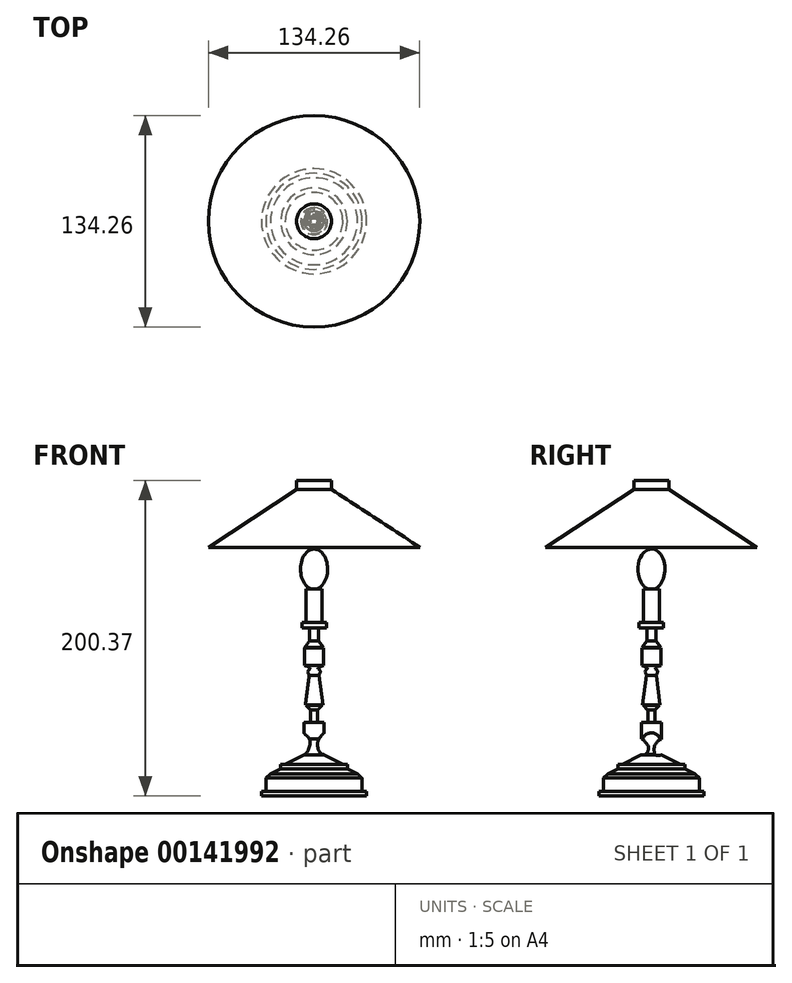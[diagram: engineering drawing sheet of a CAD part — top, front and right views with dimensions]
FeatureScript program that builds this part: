
annotation { "Feature Type Name" : "Feature", "Feature Type Description" : "" }
export const myFeature = defineFeature(function(context is Context, id is Id, definition is map)
    precondition{}
    {
        {
            var Q0;
            Q0=qCreatedBy(makeId("Right.planeOp"),FACE);
            var sketch = newSketch(context, id + "F0", { "sketchPlane" : qUnion([Q0])});
            skLineSegment(sketch, "E0", {"start": v(0, 0) * mm, "end": v(-33.4, 0) * mm});
            skLineSegment(sketch, "E1", {"start": v(-33.4, 0) * mm, "end": v(-33.4, 2.94) * mm});
            skLineSegment(sketch, "E2", {"start": v(-33.4, 2.94) * mm, "end": v(0, 2.94) * mm});
            skLineSegment(sketch, "E3", {"start": v(-30.54, 2.94) * mm, "end": v(-30.54, 11.3) * mm});
            skLineSegment(sketch, "E4", {"start": v(-30.54, 11.3) * mm, "end": v(-27.63, 14.04) * mm});
            skLineSegment(sketch, "E5", {"start": v(-27.63, 14.04) * mm, "end": v(-21.15, 17.21) * mm});
            skLineSegment(sketch, "E6", {"start": v(-21.15, 17.21) * mm, "end": v(-21.15, 20.02) * mm});
            skLineSegment(sketch, "E7", {"start": v(-21.15, 20.02) * mm, "end": v(-18.3, 20.02) * mm});
            skLineSegment(sketch, "E8", {"start": v(-18.3, 20.02) * mm, "end": v(0, 29.2) * mm});
            skLineSegment(sketch, "E9", {"start": v(0, 29.2) * mm, "end": v(0, 0) * mm, "construction": true});
            skLineSegment(sketch, "E10", {"start": v(0, 29.2) * mm, "end": v(0, 0) * mm});
            skSolve(sketch);
        }
        {
            var Q0;
            Q0 = qSketchRegion(id + "F0", true);
            var Q1;
            Q1=sQuery(id+"F0.wireOp",EDGE,"E9");
            revolve(context, id + "F1", {"entities" : qUnion([Q0]), "axis" : qUnion([Q1]), "revolveType" : RevolveType.FULL});
        }
        {
            var Q0;
            Q0=qCreatedBy(makeId("Top.planeOp"),FACE);
            var sketch = newSketch(context, id + "F2", { "sketchPlane" : qUnion([Q0])});
            skCircle(sketch, "E11", {"center": v(0, 0) * mm, "radius": 6.35 * mm});
            skSolve(sketch);
        }
        {
            var Q0;
            Q0=makeQuery(id+"F2.imprint","IMPRINT",FACE,{"disambiguationData":[TD([[makeQuery(id+"F2.imprint","IMPRINT",EDGE,{"derivedFrom":sQuery(id+"F2.wireOp",EDGE,"E11")}),1.0]])]});
            extrude(context, id + "F3", {"entities" : qUnion([Q0]), "operationType" : NewBodyOperationType.ADD, "depth" : 46.58 * mm});
        }
        {
            var Q0;
            Q0=qCreatedBy(makeId("Front.planeOp"),FACE);
            var sketch = newSketch(context, id + "F4", { "sketchPlane" : qUnion([Q0])});
            skFitSpline(sketch, "E12", {"points": [v(-6.5, 25.92) * mm, v(-4.66, 27.62) * mm, v(-3.3, 30.32) * mm, v(-2.6, 35.33) * mm, v(-6.55, 39.96) * mm], "startDerivative": vector(8.64, 7.9) * mm, "endDerivative": vector(-14.65, 14.58) * mm});
            skFitSpline(sketch, "E13", {"points": [v(6.92, 25.94) * mm, v(4.8, 26.66) * mm, v(2.74, 29.61) * mm, v(2.62, 34.96) * mm, v(6.74, 40.41) * mm], "startDerivative": vector(-7.62, 8.28) * mm, "endDerivative": vector(12.58, 12.59) * mm});
            skLineSegment(sketch, "E14", {"start": v(-6.55, 39.96) * mm, "end": v(-6.5, 25.92) * mm});
            skLineSegment(sketch, "E15", {"start": v(6.92, 25.94) * mm, "end": v(6.74, 40.41) * mm});
            skSolve(sketch);
        }
        {
            var Q0;
            Q0 = qSketchRegion(id + "F4", true);
            extrude(context, id + "F5", {"entities" : qUnion([Q0]), "operationType" : NewBodyOperationType.REMOVE, "endBound" : BoundingType.SYMMETRIC, "oppositeDirection" : true, "depth" : 25.4 * mm});
        }
        {
            var Q0;
            Q0=qCreatedBy(makeId("Right.planeOp"),FACE);
            var sketch = newSketch(context, id + "F6", { "sketchPlane" : qUnion([Q0])});
            skFitSpline(sketch, "E16", {"points": [v(-5.83, 25.94) * mm, v(-4.43, 25.98) * mm, v(-2.38, 27.95) * mm, v(-2.14, 31.86) * mm, v(-4.6, 34.93) * mm, v(-6.5, 36) * mm, v(-6.9, 26.33) * mm, v(-5.83, 25.94) * mm]});
            skFitSpline(sketch, "E17", {"points": [v(3.6, 25.85) * mm, v(2.3, 26.06) * mm, v(1.8, 28.2) * mm, v(2.09, 32.01) * mm, v(4.3, 34.89) * mm, v(6.67, 35.62) * mm, v(7.33, 26.86) * mm, v(3.6, 25.85) * mm]});
            skSolve(sketch);
        }
        {
            var Q0;
            Q0=makeQuery(id+"F6.imprint","IMPRINT",FACE,{"disambiguationData":[TD([[makeQuery(id+"F6.imprint","IMPRINT",EDGE,{"derivedFrom":sQuery(id+"F6.wireOp",EDGE,"E16")}),1.0]])]});
            var Q1;
            Q1=makeQuery(id+"F6.imprint","IMPRINT",FACE,{"disambiguationData":[TD([[makeQuery(id+"F6.imprint","IMPRINT",EDGE,{"derivedFrom":sQuery(id+"F6.wireOp",EDGE,"E17")}),-1.0]])]});
            extrude(context, id + "F7", {"entities" : qUnion([Q0, Q1]), "operationType" : NewBodyOperationType.REMOVE, "endBound" : BoundingType.SYMMETRIC, "oppositeDirection" : true, "depth" : 25.4 * mm});
        }
        {
            var Q0;
            Q0=makeQuery(id+"F3.opExtrude","CAP_FACE",FACE,{"disambiguationData":[OSD([sQuery(id+"F2.wireOp",EDGE,"E11")])],"isStart":false});
            var sketch = newSketch(context, id + "F8", { "sketchPlane" : qUnion([Q0])});
            skCircle(sketch, "E18", {"center": v(0, 0) * mm, "radius": 2.12 * mm});
            skSolve(sketch);
        }
        {
            var Q0;
            Q0 = qSketchRegion(id + "F8", true);
            extrude(context, id + "F9", {"entities" : qUnion([Q0]), "operationType" : NewBodyOperationType.ADD, "depth" : 8.08 * mm});
        }
        {
            var Q0;
            Q0=qCreatedBy(makeId("Right.planeOp"),FACE);
            var sketch = newSketch(context, id + "F10", { "sketchPlane" : qUnion([Q0])});
            skLineSegment(sketch, "E19", {"start": v(0, 54.6) * mm, "end": v(2.4, 54.6) * mm});
            skLineSegment(sketch, "E20", {"start": v(2.4, 54.6) * mm, "end": v(5.1, 57.53) * mm});
            skLineSegment(sketch, "E21", {"start": v(5.1, 57.53) * mm, "end": v(0, 57.53) * mm});
            skLineSegment(sketch, "E22", {"start": v(0, 57.53) * mm, "end": v(0, 54.6) * mm});
            skSolve(sketch);
        }
        {
            var Q0;
            Q0=makeQuery(id+"F10.imprint","IMPRINT",FACE,{"disambiguationData":[TD([[makeQuery(id+"F10.imprint","IMPRINT",EDGE,{"derivedFrom":sQuery(id+"F10.wireOp",EDGE,"E19")}),1.0]])]});
            var Q1;
            Q1=sQuery(id+"F10.wireOp",EDGE,"E22");
            revolve(context, id + "F11", {"operationType" : NewBodyOperationType.ADD, "entities" : qUnion([Q0]), "axis" : qUnion([Q1]), "revolveType" : RevolveType.FULL});
        }
        {
            var Q0;
            Q0=qCreatedBy(makeId("Right.planeOp"),FACE);
            var sketch = newSketch(context, id + "F12", { "sketchPlane" : qUnion([Q0])});
            skLineSegment(sketch, "E23", {"start": v(0, 57.73) * mm, "end": v(5.55, 57.73) * mm});
            skLineSegment(sketch, "E24", {"start": v(5.55, 57.73) * mm, "end": v(0, 99.6) * mm});
            skLineSegment(sketch, "E25", {"start": v(0, 99.6) * mm, "end": v(-6.13, 99.6) * mm});
            skLineSegment(sketch, "E26", {"start": v(-6.13, 99.6) * mm, "end": v(-6.13, 57.7) * mm});
            skLineSegment(sketch, "E27", {"start": v(-6.13, 57.7) * mm, "end": v(0, 57.73) * mm});
            skLineSegment(sketch, "E28", {"start": v(0, 57.73) * mm, "end": v(0, 99.6) * mm});
            skSolve(sketch);
        }
        {
            var Q0;
            Q0=makeQuery(id+"F12.imprint","IMPRINT",FACE,{"disambiguationData":[TD([[makeQuery(id+"F12.imprint","IMPRINT",EDGE,{"derivedFrom":sQuery(id+"F12.wireOp",EDGE,"E23")}),1.0]])]});
            var Q1;
            Q1=sQuery(id+"F12.wireOp",EDGE,"E28");
            revolve(context, id + "F13", {"entities" : qUnion([Q0]), "axis" : qUnion([Q1]), "revolveType" : RevolveType.FULL});
        }
        {
            var Q0;
            Q0=qCreatedBy(makeId("Right.planeOp"),FACE);
            var sketch = newSketch(context, id + "F14", { "sketchPlane" : qUnion([Q0])});
            skLineSegment(sketch, "E29", {"start": v(3.27, 76.39) * mm, "end": v(-3.3, 76.39) * mm});
            skLineSegment(sketch, "E30", {"start": v(3.27, 76.39) * mm, "end": v(3.27, 77.06) * mm});
            skLineSegment(sketch, "E31", {"start": v(3.27, 77.06) * mm, "end": v(-3.06, 77.06) * mm});
            skLineSegment(sketch, "E32", {"start": v(-3.06, 77.06) * mm, "end": v(-3.3, 76.39) * mm});
            skSolve(sketch);
        }
        {
            var Q0;
            Q0=makeQuery(id+"F14.imprint","IMPRINT",FACE,{"disambiguationData":[TD([[makeQuery(id+"F14.imprint","IMPRINT",EDGE,{"derivedFrom":sQuery(id+"F14.wireOp",EDGE,"E29")}),-1.0]])]});
            extrude(context, id + "F15", {"entities" : qUnion([Q0]), "operationType" : NewBodyOperationType.REMOVE, "endBound" : BoundingType.SYMMETRIC, "oppositeDirection" : true, "depth" : 25.4 * mm});
        }
        {
            var Q0;
            Q0=makeQuery(id+"F15.boolean.opBoolean","COPY",FACE,{"derivedFrom":makeQuery(id+"F15.opExtrude","SWEPT_FACE",FACE,{"disambiguationData":[OSD([sQuery(id+"F14.wireOp",EDGE,"E31")])]})});
            extrude(context, id + "F16", {"entities" : qUnion([Q0]), "operationType" : NewBodyOperationType.REMOVE, "oppositeDirection" : true, "depth" : 25.4 * mm});
        }
        {
            var Q0;
            Q0=qCreatedBy(makeId("Right.planeOp"),FACE);
            var sketch = newSketch(context, id + "F17", { "sketchPlane" : qUnion([Q0])});
            skFitSpline(sketch, "E33", {"points": [v(2.64, 76.27) * mm, v(3.93, 79.26) * mm, v(2.55, 81.11) * mm, v(6.1, 82.82) * mm], "startDerivative": vector(7.13, 9.32) * mm, "endDerivative": vector(14.33, 4.15) * mm});
            skLineSegment(sketch, "E34", {"start": v(6.1, 82.82) * mm, "end": v(6.1, 100.57) * mm});
            skLineSegment(sketch, "E35", {"start": v(6.1, 100.57) * mm, "end": v(0, 100.57) * mm});
            skLineSegment(sketch, "E36", {"start": v(0, 100.57) * mm, "end": v(0, 76.2) * mm, "construction": true});
            skLineSegment(sketch, "E37", {"start": v(0, 76.2) * mm, "end": v(2.64, 76.27) * mm});
            skLineSegment(sketch, "E38", {"start": v(0, 100.57) * mm, "end": v(0, 76.2) * mm});
            skSolve(sketch);
        }
        {
            var Q0;
            Q0 = qSketchRegion(id + "F17", true);
            var Q1;
            Q1=sQuery(id+"F17.wireOp",EDGE,"E36");
            revolve(context, id + "F18", {"entities" : qUnion([Q0]), "axis" : qUnion([Q1]), "revolveType" : RevolveType.FULL});
        }
        {
            var Q0;
            Q0=makeQuery(id+"F18.opRevolve","SWEPT_FACE",FACE,{"disambiguationData":[OSD([sQuery(id+"F17.wireOp",EDGE,"E35")])]});
            extrude(context, id + "F19", {"entities" : qUnion([Q0]), "operationType" : NewBodyOperationType.REMOVE, "oppositeDirection" : true, "depth" : 6.52 * mm});
        }
        {
            var Q0;
            Q0=qCreatedBy(makeId("Right.planeOp"),FACE);
            var sketch = newSketch(context, id + "F20", { "sketchPlane" : qUnion([Q0])});
            skLineSegment(sketch, "E39", {"start": v(5.93, 94.24) * mm, "end": v(0, 102.57) * mm});
            skLineSegment(sketch, "E40", {"start": v(0, 102.57) * mm, "end": v(0, 106.82) * mm});
            skLineSegment(sketch, "E41", {"start": v(0, 106.82) * mm, "end": v(7.8, 106.82) * mm});
            skLineSegment(sketch, "E42", {"start": v(7.8, 106.82) * mm, "end": v(7.8, 110.13) * mm});
            skLineSegment(sketch, "E43", {"start": v(7.8, 110.13) * mm, "end": v(0, 110.13) * mm});
            skLineSegment(sketch, "E44", {"start": v(0, 110.13) * mm, "end": v(0, 106.82) * mm});
            skLineSegment(sketch, "E45", {"start": v(0, 102.57) * mm, "end": v(0, 93.56) * mm});
            skLineSegment(sketch, "E46", {"start": v(0, 93.56) * mm, "end": v(5.93, 94.24) * mm});
            skLineSegment(sketch, "E47", {"start": v(0, 102.57) * mm, "end": v(2.96, 102.57) * mm});
            skPoint(sketch, "E47.endSnap0", {"position": v(2.96, 98.4) * mm});
            skLineSegment(sketch, "E48", {"start": v(2.96, 102.57) * mm, "end": v(2.96, 106.82) * mm});
            skPoint(sketch, "E48.endSnap0", {"position": v(3.9, 106.82) * mm});
            skLineSegment(sketch, "E49", {"start": v(2.96, 106.82) * mm, "end": v(2.96, 102.57) * mm});
            skLineSegment(sketch, "E50", {"start": v(2.96, 98.4) * mm, "end": v(2.96, 102.57) * mm});
            skSolve(sketch);
        }
        {
            var Q0;
            Q0 = qSketchRegion(id + "F20", true);
            var Q1;
            Q1=sQuery(id+"F20.wireOp",EDGE,"E40");
            revolve(context, id + "F21", {"operationType" : NewBodyOperationType.ADD, "entities" : qUnion([Q0]), "axis" : qUnion([Q1]), "revolveType" : RevolveType.FULL});
        }
        {
            var Q0;
            Q0=makeQuery(id+"F21.opRevolve","SWEPT_FACE",FACE,{"disambiguationData":[OSD([sQuery(id+"F20.wireOp",EDGE,"E43")])]});
            var sketch = newSketch(context, id + "F22", { "sketchPlane" : qUnion([Q0])});
            skCircle(sketch, "E51", {"center": v(0, 0) * mm, "radius": 5.18 * mm});
            skSolve(sketch);
        }
        {
            var Q0;
            Q0=makeQuery(id+"F22.imprint","IMPRINT",FACE,{"disambiguationData":[TD([[makeQuery(id+"F22.imprint","IMPRINT",EDGE,{"derivedFrom":sQuery(id+"F22.wireOp",EDGE,"E51")}),1.0]])]});
            extrude(context, id + "F23", {"entities" : qUnion([Q0]), "operationType" : NewBodyOperationType.ADD, "depth" : 21.32 * mm});
        }
        {
            var Q0;
            Q0=qCreatedBy(makeId("Right.planeOp"),FACE);
            var sketch = newSketch(context, id + "F24", { "sketchPlane" : qUnion([Q0])});
            skEllipse(sketch, "E52", {"center": v(0, 144.02) * mm, "majorRadius": 12.83 * mm, "minorRadius": 8.61 * mm, "majorAxis": v(0, 1)});
            skLineSegment(sketch, "E53", {"start": v(0, 144.02) * mm, "end": v(0, 131.18) * mm});
            skLineSegment(sketch, "E54", {"start": v(0, 131.18) * mm, "end": v(0, 156.85) * mm});
            skSolve(sketch);
        }
        {
            var Q0;
            {var subQ0=sQuery(id+"F24.wireOp",EDGE,"E54");var subQ4=makeQuery(id+"F24.imprint","IMPRINT",VERTEX,{"derivedFrom":subQ0});Q0=makeQuery(id+"F24.imprint","IMPRINT",FACE,{"disambiguationData":[TD([[makeQuery(id+"F24.imprint","IMPRINT",EDGE,{"disambiguationData":[TD([[subQ4,1.0]])],"derivedFrom":subQ0}),-1.0]])]});}
            var Q1;
            Q1=sQuery(id+"F24.wireOp",EDGE,"E54");
            revolve(context, id + "F25", {"entities" : qUnion([Q0]), "axis" : qUnion([Q1]), "revolveType" : RevolveType.FULL});
        }
        {
            var Q0;
            Q0=qCreatedBy(makeId("Right.planeOp"),FACE);
            var sketch = newSketch(context, id + "F26", { "sketchPlane" : qUnion([Q0])});
            skLineSegment(sketch, "E55", {"start": v(0, 157.96) * mm, "end": v(67.13, 157.96) * mm});
            skLineSegment(sketch, "E56", {"start": v(67.13, 157.96) * mm, "end": v(11.05, 194.62) * mm});
            skLineSegment(sketch, "E57", {"start": v(11.05, 194.62) * mm, "end": v(11.05, 200.37) * mm});
            skLineSegment(sketch, "E58", {"start": v(11.05, 200.37) * mm, "end": v(0, 200.37) * mm});
            skLineSegment(sketch, "E59", {"start": v(0, 200.37) * mm, "end": v(0, 157.96) * mm});
            skLineSegment(sketch, "E60", {"start": v(16.43, 157.96) * mm, "end": v(16.43, 146.95) * mm});
            skLineSegment(sketch, "E61", {"start": v(16.43, 146.95) * mm, "end": v(0, 146.95) * mm});
            skLineSegment(sketch, "E62", {"start": v(0, 146.95) * mm, "end": v(0, 157.96) * mm});
            skSolve(sketch);
        }
        {
            var Q0;
            {var subQ0=sQuery(id+"F26.wireOp",EDGE,"E56");Q0=makeQuery(id+"F26.imprint","IMPRINT",FACE,{"disambiguationData":[TD([[makeQuery(id+"F26.imprint","IMPRINT",EDGE,{"derivedFrom":subQ0}),1.0]])]});}
            var Q1;
            Q1=sQuery(id+"F26.wireOp",EDGE,"E59");
            revolve(context, id + "F27", {"entities" : qUnion([Q0]), "axis" : qUnion([Q1]), "revolveType" : RevolveType.FULL});
        }
        {
            var Q0;
            Q0=sQuery(id+"F26.wireOp",EDGE,"E60");
            var Q1;
            Q1=sQuery(id+"F26.wireOp",EDGE,"E61");
            var Q2;
            Q2=sQuery(id+"F26.wireOp",EDGE,"E59");
            revolve(context, id + "F28", {"bodyType" : ToolBodyType.SURFACE, "surfaceEntities" : qUnion([Q0, Q1]), "axis" : qUnion([Q2]), "revolveType" : RevolveType.FULL});
        }
    });
